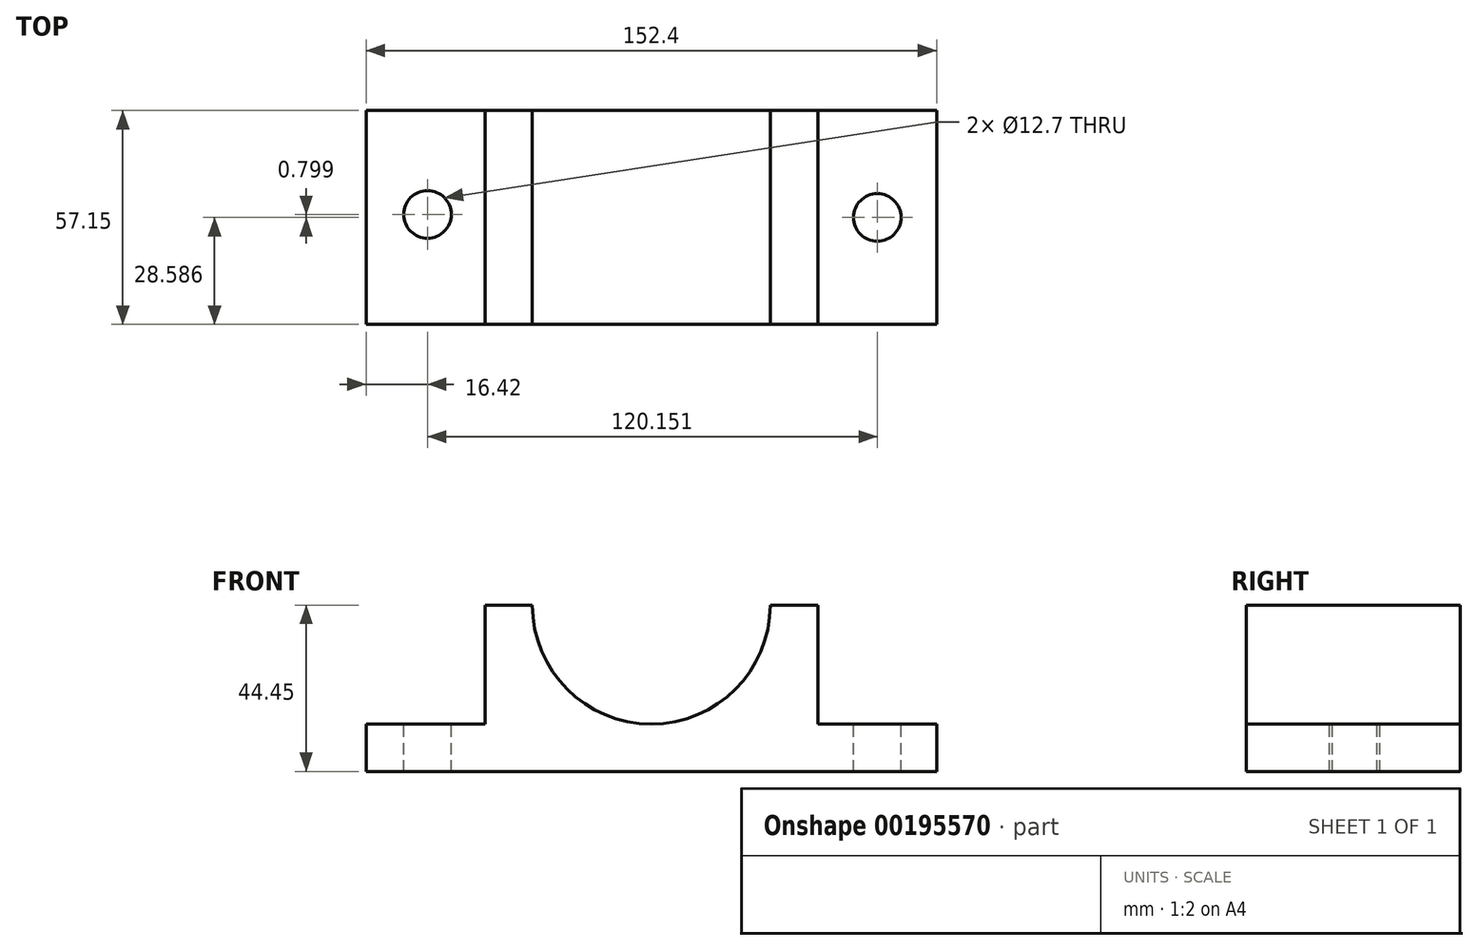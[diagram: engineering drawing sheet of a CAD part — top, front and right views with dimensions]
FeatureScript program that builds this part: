
annotation { "Feature Type Name" : "Feature", "Feature Type Description" : "" }
export const myFeature = defineFeature(function(context is Context, id is Id, definition is map)
    precondition{}
    {
        {
            var Q0;
            Q0=qCreatedBy(makeId("Front.planeOp"),FACE);
            var sketch = newSketch(context, id + "F0", { "sketchPlane" : qUnion([Q0])});
            skLineSegment(sketch, "E0", {"start": v(-868.6, 108.32) * mm, "end": v(-868.6, 95.62) * mm});
            skLineSegment(sketch, "E1", {"start": v(-868.6, 95.62) * mm, "end": v(-792.4, 95.62) * mm});
            skLineSegment(sketch, "E2", {"start": v(-716.2, 95.62) * mm, "end": v(-716.2, 108.32) * mm});
            skLineSegment(sketch, "E3", {"start": v(-868.6, 95.62) * mm, "end": v(-868.6, 108.32) * mm});
            skLineSegment(sketch, "E4", {"start": v(-868.6, 108.32) * mm, "end": v(-836.85, 108.32) * mm});
            skLineSegment(sketch, "E5", {"start": v(-836.85, 140.07) * mm, "end": v(-836.85, 108.32) * mm});
            skLineSegment(sketch, "E6", {"start": v(-747.95, 140.07) * mm, "end": v(-747.95, 108.32) * mm});
            skLineSegment(sketch, "E7", {"start": v(-792.4, 108.3) * mm, "end": v(-792.4, 108.32) * mm});
            skLineSegment(sketch, "E8", {"start": v(-792.4, 95.62) * mm, "end": v(-716.2, 95.62) * mm});
            skArc(sketch, "E9", {"start": v(-824.17, 140.07) * mm, "mid": v(-792.4, 108.3) * mm, "end": v(-760.63, 140.07) * mm});
            skLineSegment(sketch, "E10", {"start": v(-836.85, 140.07) * mm, "end": v(-824.17, 140.07) * mm});
            skLineSegment(sketch, "E11", {"start": v(-747.95, 140.07) * mm, "end": v(-760.63, 140.07) * mm});
            skLineSegment(sketch, "E12.trimOffspring", {"start": v(-747.95, 108.32) * mm, "end": v(-716.2, 108.32) * mm});
            skLineSegment(sketch, "E13.trimOffspring", {"start": v(-793.43, 108.32) * mm, "end": v(-791.37, 108.32) * mm});
            skSolve(sketch);
        }
        {
            var Q0;
            Q0=makeQuery(id+"F0.imprint","IMPRINT",FACE,{"disambiguationData":[TD([[makeQuery(id+"F0.imprint","IMPRINT",EDGE,{"derivedFrom":sQuery(id+"F0.wireOp",EDGE,"E1")}),1.0]])]});
            extrude(context, id + "F1", {"entities" : qUnion([Q0]), "depth" : 57.15 * mm});
        }
        {
            var Q0;
            Q0=makeQuery(id+"F1.opExtrude","SWEPT_FACE",FACE,{"disambiguationData":[OSD([sQuery(id+"F0.wireOp",EDGE,"E4")])]});
            cPlane(context, id + "F2", {"entities" : qUnion([Q0]), "cplaneType" : CPlaneType.OFFSET, "offset" : 0 * mm, "width" : 152.4 * mm, "height" : 152.4 * mm});
        }
        {
            var Q0;
            Q0=qCreatedBy(id+"F2.planeOp",FACE);
            var sketch = newSketch(context, id + "F3", { "sketchPlane" : qUnion([Q0])});
            skCircle(sketch, "E14", {"center": v(-852.18, -27.77) * mm, "radius": 6.35 * mm});
            skSolve(sketch);
        }
        {
            var Q0;
            Q0=makeQuery(id+"F3.imprint","IMPRINT",FACE,{"disambiguationData":[TD([[makeQuery(id+"F3.imprint","IMPRINT",EDGE,{"derivedFrom":sQuery(id+"F3.wireOp",EDGE,"E14")}),1.0]])]});
            extrude(context, id + "F4", {"entities" : qUnion([Q0]), "operationType" : NewBodyOperationType.REMOVE, "oppositeDirection" : true, "depth" : 12.7 * mm});
        }
        {
            var Q0;
            Q0=makeQuery(id+"F1.opExtrude","SWEPT_FACE",FACE,{"disambiguationData":[OSD([sQuery(id+"F0.wireOp",EDGE,"E12.trimOffspring")])]});
            cPlane(context, id + "F5", {"entities" : qUnion([Q0]), "cplaneType" : CPlaneType.OFFSET, "offset" : 0 * mm, "width" : 152.4 * mm, "height" : 152.4 * mm});
        }
        {
            var Q0;
            Q0=qCreatedBy(id+"F5.planeOp",FACE);
            var sketch = newSketch(context, id + "F6", { "sketchPlane" : qUnion([Q0])});
            skPoint(sketch, "E15.end.orphan", {"position": v(-732.03, 0) * mm});
            skPoint(sketch, "E16.start.orphan", {"position": v(-716.15, 0) * mm});
            skCircle(sketch, "E17", {"center": v(-732.03, -28.56) * mm, "radius": 6.35 * mm});
            skSolve(sketch);
        }
        {
            var Q0;
            Q0=makeQuery(id+"F6.imprint","IMPRINT",FACE,{"disambiguationData":[TD([[makeQuery(id+"F6.imprint","IMPRINT",EDGE,{"derivedFrom":sQuery(id+"F6.wireOp",EDGE,"E17")}),1.0]])]});
            extrude(context, id + "F7", {"entities" : qUnion([Q0]), "operationType" : NewBodyOperationType.REMOVE, "oppositeDirection" : true, "depth" : 12.7 * mm});
        }
    });
